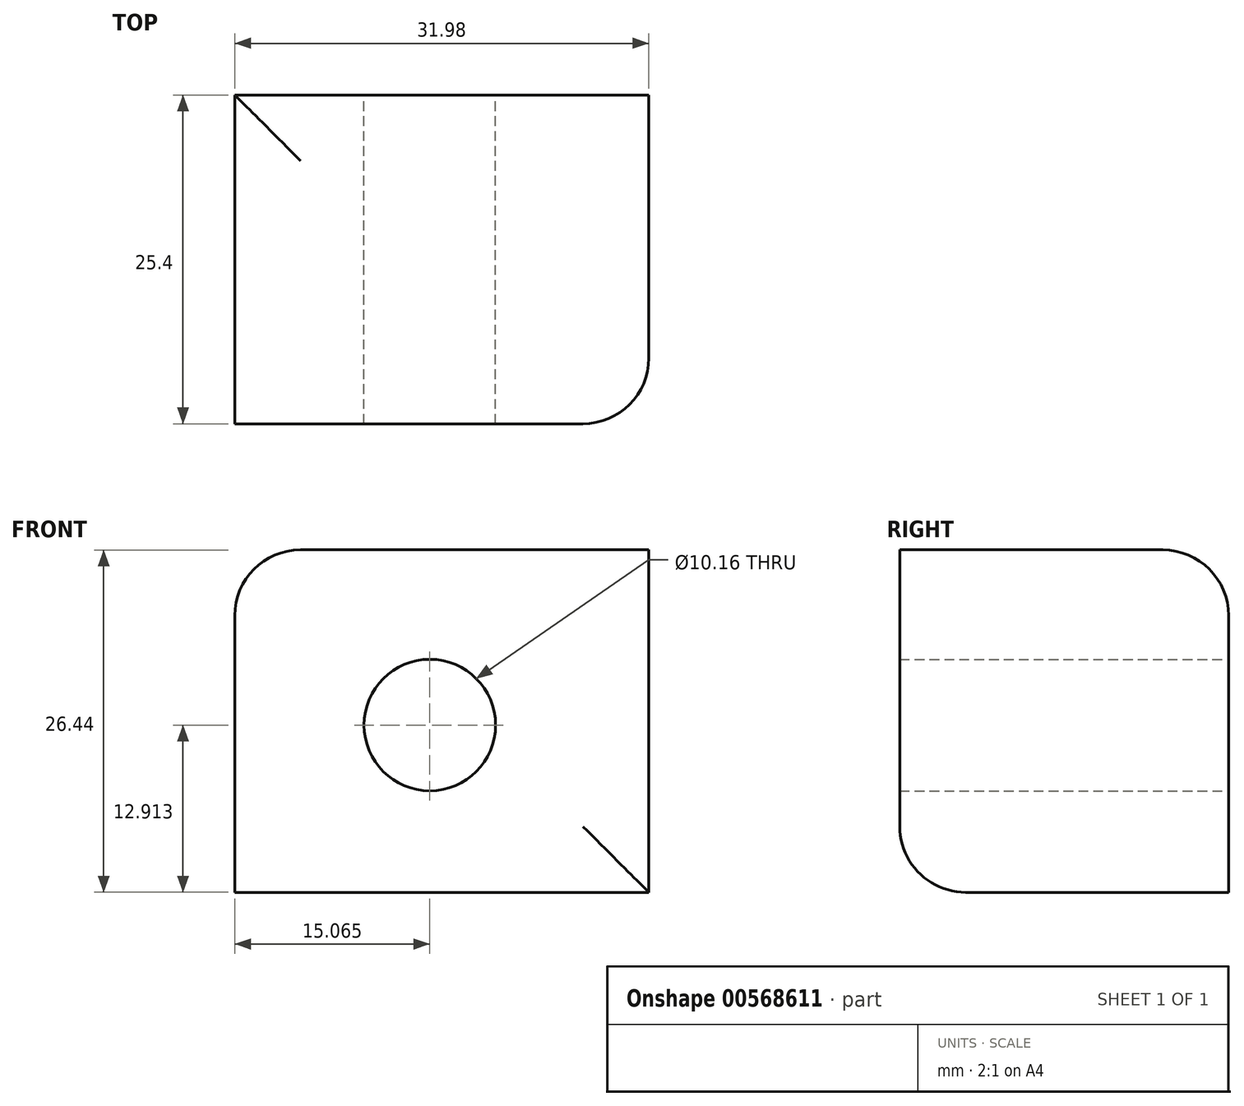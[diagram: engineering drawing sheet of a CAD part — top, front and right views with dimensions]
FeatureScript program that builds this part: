
annotation { "Feature Type Name" : "Feature", "Feature Type Description" : "" }
export const myFeature = defineFeature(function(context is Context, id is Id, definition is map)
    precondition{}
    {
        {
            var Q0;
            Q0=qCreatedBy(makeId("Front.planeOp"),FACE);
            var sketch = newSketch(context, id + "F0", { "sketchPlane" : qUnion([Q0])});
            skCircle(sketch, "E0", {"center": v(-39.37, 39.67) * mm, "radius": 5.08 * mm});
            skLineSegment(sketch, "E1.bottom", {"start": v(-54.43, 53.2) * mm, "end": v(-22.45, 53.2) * mm});
            skLineSegment(sketch, "E1.top", {"start": v(-54.43, 26.76) * mm, "end": v(-22.45, 26.76) * mm});
            skLineSegment(sketch, "E1.left", {"start": v(-54.43, 53.2) * mm, "end": v(-54.43, 26.76) * mm});
            skLineSegment(sketch, "E1.right", {"start": v(-22.45, 53.2) * mm, "end": v(-22.45, 26.76) * mm});
            skSolve(sketch);
        }
        {
            var Q0;
            Q0=makeQuery(id+"F0.imprint","IMPRINT",FACE,{"disambiguationData":[TD([[makeQuery(id+"F0.imprint","IMPRINT",EDGE,{"derivedFrom":sQuery(id+"F0.wireOp",EDGE,"E0")}),-1.0]])]});
            extrude(context, id + "F1", {"entities" : qUnion([Q0]), "endBound" : BoundingType.SYMMETRIC, "depth" : 25.4 * mm, "offsetDistance" : 25.4 * mm});
        }
        {
            var Q0;
            Q0=makeQuery(id+"F1.opExtrude","CAP_EDGE",EDGE,{"disambiguationData":[OSD([sQuery(id+"F0.wireOp",EDGE,"E1.bottom")])],"isStart":true});
            var Q1;
            Q1=makeQuery(id+"F1.opExtrude","SWEPT_EDGE",EDGE,{"disambiguationData":[OSD([sQuery(id+"F0.wireOp",EDGE,"E1.bottom"),sQuery(id+"F0.wireOp",EDGE,"E1.left")])]});
            var Q2;
            Q2=makeQuery(id+"F1.opExtrude","CAP_EDGE",EDGE,{"disambiguationData":[OSD([sQuery(id+"F0.wireOp",EDGE,"E1.right")])],"isStart":false});
            var Q3;
            Q3=makeQuery(id+"F1.opExtrude","CAP_EDGE",EDGE,{"disambiguationData":[OSD([sQuery(id+"F0.wireOp",EDGE,"E1.top")])],"isStart":false});
            fillet(context, id + "F2", {"entities" : qUnion([Q0, Q1, Q2, Q3]), "radius" : 5.08 * mm, "tangentPropagation" : true, "allowEdgeOverflow" : false});
        }
    });
